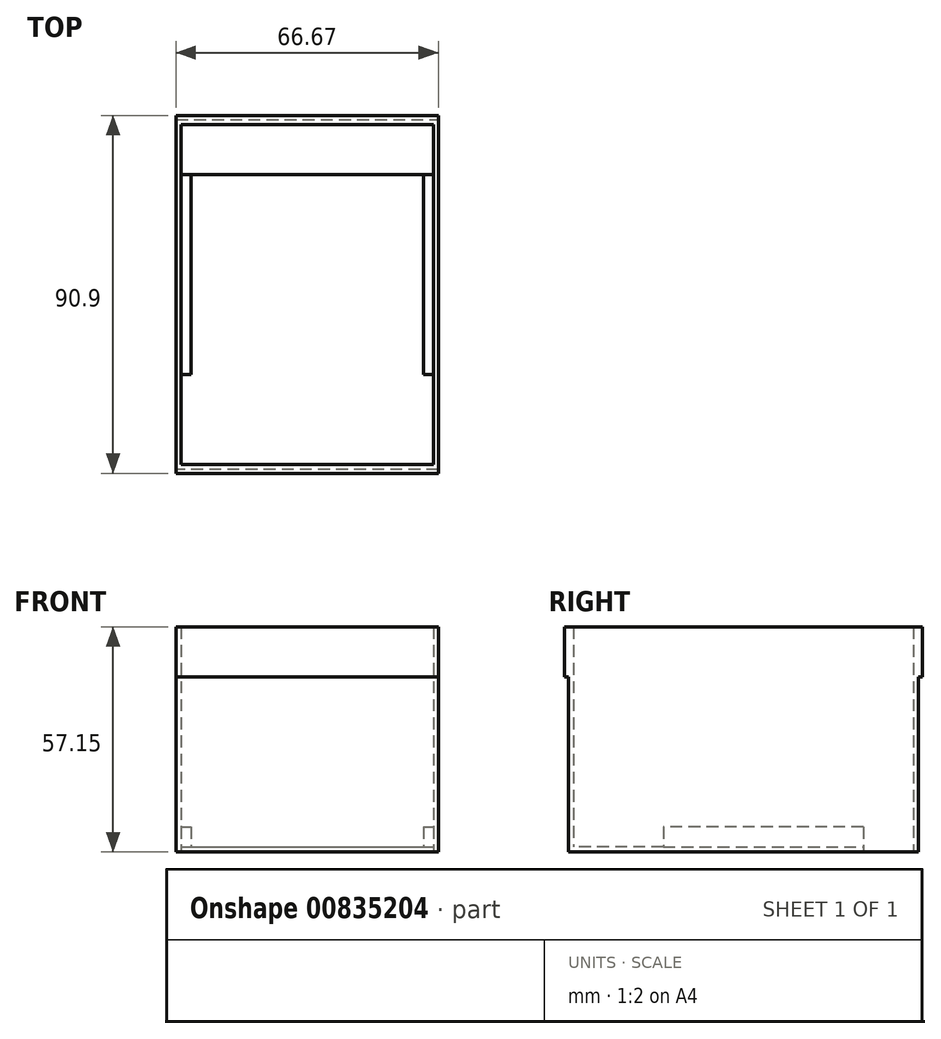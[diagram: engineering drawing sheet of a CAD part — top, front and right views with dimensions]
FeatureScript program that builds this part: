
annotation { "Feature Type Name" : "Feature", "Feature Type Description" : "" }
export const myFeature = defineFeature(function(context is Context, id is Id, definition is map)
    precondition{}
    {
        {
            var Q0;
            Q0=qCreatedBy(makeId("Top.planeOp"),FACE);
            var sketch = newSketch(context, id + "F0", { "sketchPlane" : qUnion([Q0])});
            skLineSegment(sketch, "E0.bottom", {"start": v(-34.46, 55.3) * mm, "end": v(32.21, 55.3) * mm});
            skLineSegment(sketch, "E0.top", {"start": v(-34.46, -33.6) * mm, "end": v(32.21, -33.6) * mm});
            skLineSegment(sketch, "E0.left", {"start": v(-34.46, 55.3) * mm, "end": v(-34.46, -33.6) * mm});
            skLineSegment(sketch, "E0.right", {"start": v(32.21, 55.3) * mm, "end": v(32.21, -33.6) * mm});
            skSolve(sketch);
        }
        {
            var Q0;
            Q0=makeQuery(id+"F0.imprint","IMPRINT",FACE,{"disambiguationData":[TD([[makeQuery(id+"F0.imprint","IMPRINT",EDGE,{"derivedFrom":sQuery(id+"F0.wireOp",EDGE,"E0.bottom")}),-1.0]])]});
            extrude(context, id + "F1", {"entities" : qUnion([Q0]), "depth" : 57.15 * mm, "offsetDistance" : 25.4 * mm});
        }
        {
            var Q0;
            Q0=makeQuery(id+"F1.opExtrude","CAP_FACE",FACE,{"disambiguationData":[OSD([sQuery(id+"F0.wireOp",EDGE,"E0.bottom"),sQuery(id+"F0.wireOp",EDGE,"E0.top"),sQuery(id+"F0.wireOp",EDGE,"E0.left"),sQuery(id+"F0.wireOp",EDGE,"E0.right")])],"isStart":false});
            shell(context, id + "F2", {"entities" : qUnion([Q0]), "thickness" : 1.27 * mm});
        }
        {
            var Q0;
            Q0=makeQuery(id+"F2.opShell","OFFSET_FACE",FACE,{"disambiguationData":[OSD([sQuery(id+"F0.wireOp",EDGE,"E0.bottom"),sQuery(id+"F0.wireOp",EDGE,"E0.top"),sQuery(id+"F0.wireOp",EDGE,"E0.left"),sQuery(id+"F0.wireOp",EDGE,"E0.right")])]});
            var sketch = newSketch(context, id + "F3", { "sketchPlane" : qUnion([Q0])});
            skLineSegment(sketch, "E1", {"start": v(-33.2, 41.34) * mm, "end": v(30.94, 41.34) * mm});
            skLineSegment(sketch, "E2", {"start": v(-33.2, -9.46) * mm, "end": v(30.94, -9.46) * mm});
            skLineSegment(sketch, "E3", {"start": v(28.4, 41.34) * mm, "end": v(28.4, -9.46) * mm});
            skLineSegment(sketch, "E4", {"start": v(-30.65, -9.46) * mm, "end": v(-30.65, 41.34) * mm});
            skLineSegment(sketch, "E5", {"start": v(-30.65, -0.2) * mm, "end": v(28.4, -0.2) * mm});
            skLineSegment(sketch, "E6", {"start": v(-30.65, -3.37) * mm, "end": v(28.4, -3.37) * mm});
            skLineSegment(sketch, "E7.top", {"start": v(-33.2, -22.16) * mm, "end": v(30.94, -22.16) * mm});
            skLineSegment(sketch, "E7.left", {"start": v(-33.2, -9.46) * mm, "end": v(-33.2, -22.16) * mm});
            skLineSegment(sketch, "E7.right", {"start": v(30.94, -9.46) * mm, "end": v(30.94, -22.16) * mm});
            skLineSegment(sketch, "E8.top", {"start": v(-33.2, 54.04) * mm, "end": v(30.94, 54.04) * mm});
            skLineSegment(sketch, "E8.left", {"start": v(-33.2, 41.34) * mm, "end": v(-33.2, 54.04) * mm});
            skLineSegment(sketch, "E8.right", {"start": v(30.94, 41.34) * mm, "end": v(30.94, 54.04) * mm});
            skSolve(sketch);
        }
        {
            var Q0;
            {var subQ4=sQuery(id+"F3.wireOp",EDGE,"E3");Q0=makeQuery(id+"F3.imprint","IMPRINT",FACE,{"disambiguationData":[TD([[makeQuery(id+"F3.imprint","IMPRINT",EDGE,{"derivedFrom":subQ4}),1.0]])]});}
            var Q1;
            {var subQ4=sQuery(id+"F3.wireOp",EDGE,"E4");Q1=makeQuery(id+"F3.imprint","IMPRINT",FACE,{"disambiguationData":[TD([[makeQuery(id+"F3.imprint","IMPRINT",EDGE,{"derivedFrom":subQ4}),1.0]])]});}
            extrude(context, id + "F4", {"entities" : qUnion([Q0, Q1]), "operationType" : NewBodyOperationType.ADD, "depth" : 5.08 * mm, "offsetDistance" : 25.4 * mm});
        }
        {
            var Q0;
            Q0=makeQuery(id+"F1.opExtrude","SWEPT_FACE",FACE,{"disambiguationData":[OSD([sQuery(id+"F0.wireOp",EDGE,"E0.bottom")])]});
            var sketch = newSketch(context, id + "F5", { "sketchPlane" : qUnion([Q0])});
            skLineSegment(sketch, "E9.bottom", {"start": v(34.46, 57.15) * mm, "end": v(-32.21, 57.15) * mm});
            skLineSegment(sketch, "E9.top", {"start": v(34.46, 44.45) * mm, "end": v(-32.21, 44.45) * mm});
            skLineSegment(sketch, "E9.left", {"start": v(34.46, 57.15) * mm, "end": v(34.46, 44.45) * mm});
            skLineSegment(sketch, "E9.right", {"start": v(-32.21, 57.15) * mm, "end": v(-32.21, 44.45) * mm});
            skSolve(sketch);
        }
        {
            var Q0;
            Q0=makeQuery(id+"F5.imprint","IMPRINT",FACE,{"disambiguationData":[TD([[makeQuery(id+"F5.imprint","IMPRINT",EDGE,{"derivedFrom":sQuery(id+"F5.wireOp",EDGE,"E9.bottom")}),1.0]])]});
            extrude(context, id + "F6", {"entities" : qUnion([Q0]), "operationType" : NewBodyOperationType.ADD, "depth" : 1 * mm, "offsetDistance" : 25.4 * mm});
        }
        {
            var Q0;
            Q0=makeQuery(id+"F1.opExtrude","SWEPT_FACE",FACE,{"disambiguationData":[OSD([sQuery(id+"F0.wireOp",EDGE,"E0.top")])]});
            var sketch = newSketch(context, id + "F7", { "sketchPlane" : qUnion([Q0])});
            skLineSegment(sketch, "E10.bottom", {"start": v(32.21, 57.15) * mm, "end": v(-34.46, 57.15) * mm});
            skLineSegment(sketch, "E10.top", {"start": v(32.21, 44.45) * mm, "end": v(-34.46, 44.45) * mm});
            skLineSegment(sketch, "E10.left", {"start": v(32.21, 57.15) * mm, "end": v(32.21, 44.45) * mm});
            skLineSegment(sketch, "E10.right", {"start": v(-34.46, 57.15) * mm, "end": v(-34.46, 44.45) * mm});
            skSolve(sketch);
        }
        {
            var Q0;
            Q0=makeQuery(id+"F7.imprint","IMPRINT",FACE,{"disambiguationData":[TD([[makeQuery(id+"F7.imprint","IMPRINT",EDGE,{"derivedFrom":sQuery(id+"F7.wireOp",EDGE,"E10.bottom")}),-1.0]])]});
            extrude(context, id + "F8", {"entities" : qUnion([Q0]), "operationType" : NewBodyOperationType.ADD, "depth" : 1 * mm, "offsetDistance" : 25.4 * mm});
        }
        {
            var Q0;
            Q0=makeQuery(id+"F3.imprint","IMPRINT",FACE,{"disambiguationData":[TD([[makeQuery(id+"F3.imprint","IMPRINT",EDGE,{"derivedFrom":sQuery(id+"F3.wireOp",EDGE,"E8.top")}),-1.0]])]});
            extrude(context, id + "F9", {"entities" : qUnion([Q0]), "operationType" : NewBodyOperationType.REMOVE, "oppositeDirection" : true, "depth" : 25.4 * mm, "offsetDistance" : 25.4 * mm});
        }
    });
